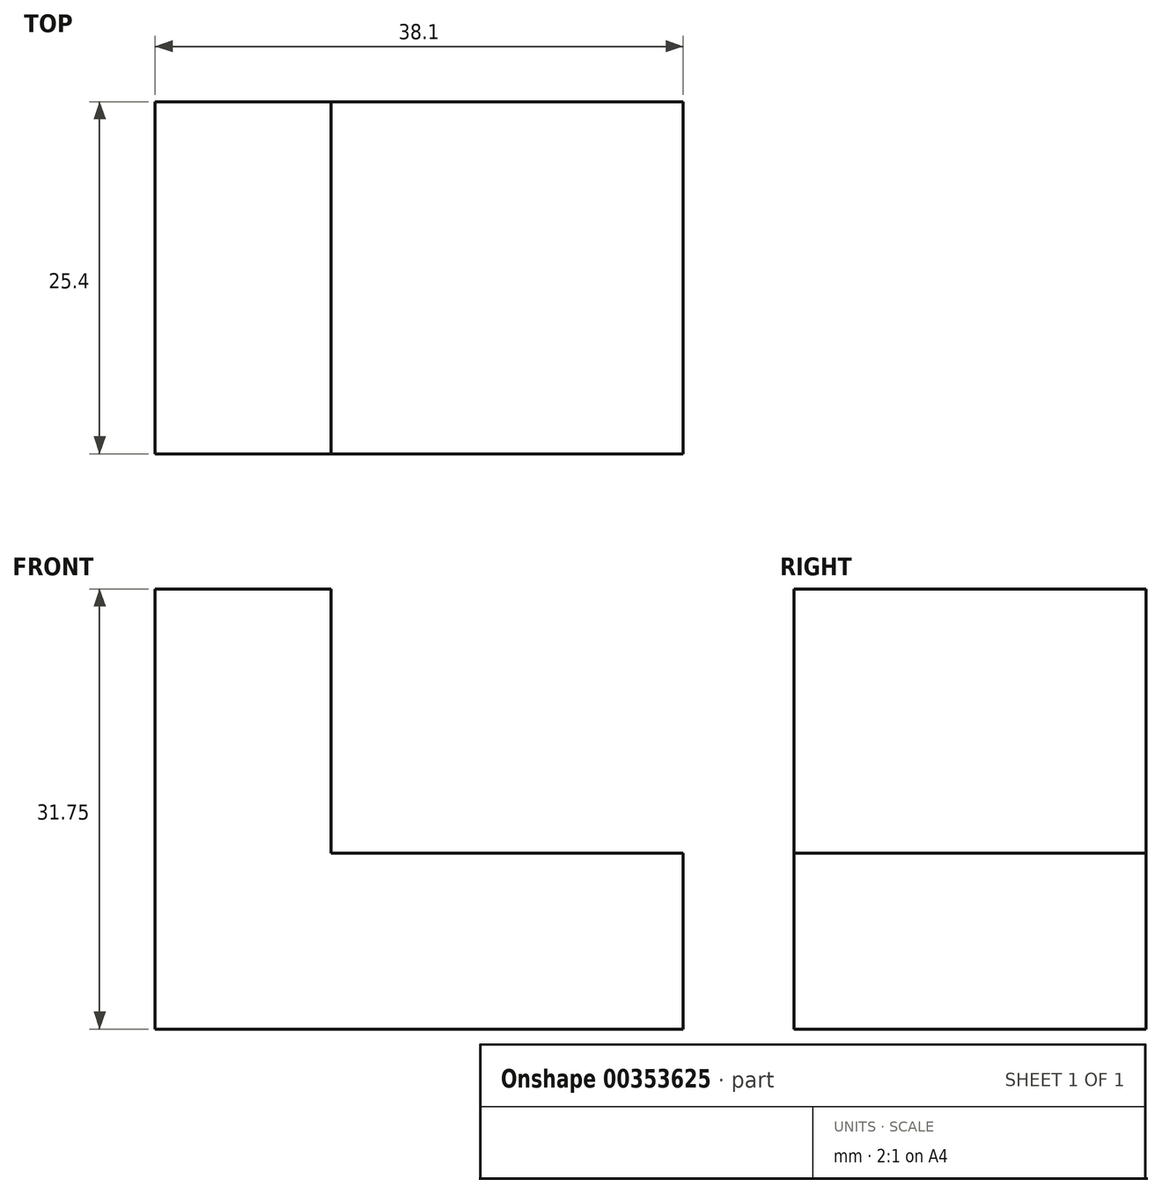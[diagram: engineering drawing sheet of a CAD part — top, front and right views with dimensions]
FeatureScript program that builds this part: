
annotation { "Feature Type Name" : "Feature", "Feature Type Description" : "" }
export const myFeature = defineFeature(function(context is Context, id is Id, definition is map)
    precondition{}
    {
        {
            var Q0;
            Q0=qCreatedBy(makeId("Front.planeOp"),FACE);
            var sketch = newSketch(context, id + "F0", { "sketchPlane" : qUnion([Q0])});
            skLineSegment(sketch, "E0", {"start": v(7.57, 44.54) * mm, "end": v(7.57, 12.8) * mm});
            skLineSegment(sketch, "E1", {"start": v(7.57, 12.8) * mm, "end": v(45.67, 12.8) * mm});
            skLineSegment(sketch, "E2", {"start": v(45.67, 12.8) * mm, "end": v(45.67, 25.5) * mm});
            skLineSegment(sketch, "E3", {"start": v(45.67, 25.5) * mm, "end": v(20.27, 25.5) * mm});
            skLineSegment(sketch, "E4", {"start": v(20.27, 25.5) * mm, "end": v(20.27, 44.54) * mm});
            skLineSegment(sketch, "E5", {"start": v(20.27, 44.54) * mm, "end": v(7.57, 44.54) * mm});
            skSolve(sketch);
        }
        {
            var Q0;
            Q0 = qSketchRegion(id + "F0", true);
            extrude(context, id + "F1", {"entities" : qUnion([Q0]), "depth" : 25.4 * mm});
        }
    });
